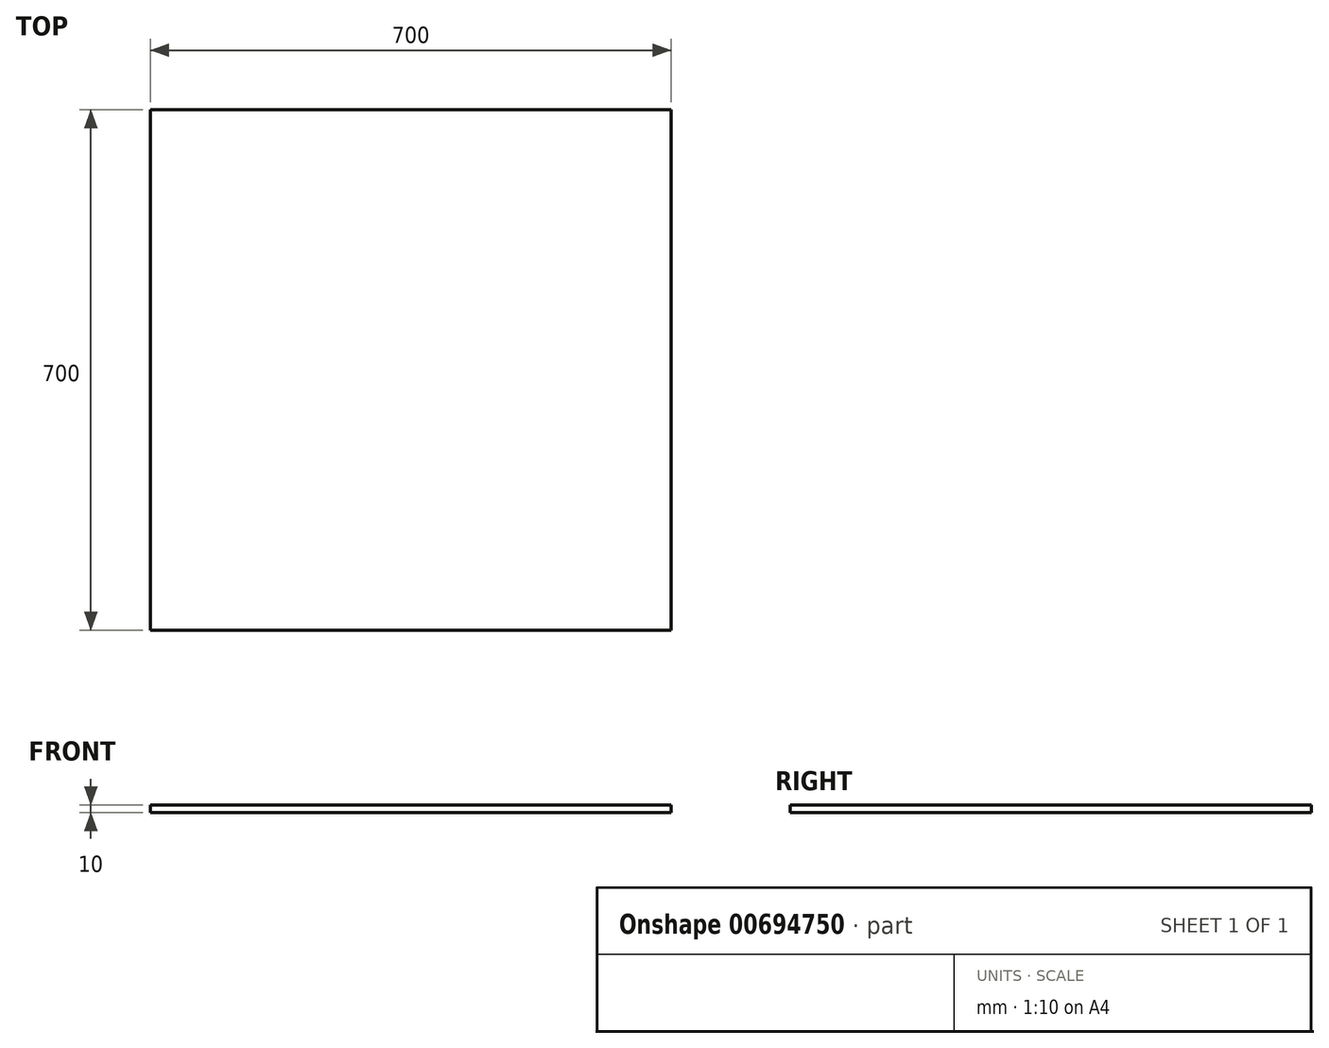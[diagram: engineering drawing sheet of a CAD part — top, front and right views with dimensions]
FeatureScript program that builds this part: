
annotation { "Feature Type Name" : "Feature", "Feature Type Description" : "" }
export const myFeature = defineFeature(function(context is Context, id is Id, definition is map)
    precondition{}
    {
        {
            var Q0;
            Q0=qCreatedBy(makeId("Top.planeOp"),FACE);
            var sketch = newSketch(context, id + "F0", { "sketchPlane" : qUnion([Q0])});
            skLineSegment(sketch, "E0.bottom", {"start": v(350, -350) * mm, "end": v(-350, -350) * mm});
            skLineSegment(sketch, "E0.top", {"start": v(350, 350) * mm, "end": v(-350, 350) * mm});
            skLineSegment(sketch, "E0.left", {"start": v(350, -350) * mm, "end": v(350, 350) * mm});
            skLineSegment(sketch, "E0.right", {"start": v(-350, -350) * mm, "end": v(-350, 350) * mm});
            skPoint(sketch, "E0.middle", {"position": v(0, 0) * mm});
            skSolve(sketch);
        }
        {
            var Q0;
            Q0 = qSketchRegion(id + "F0", true);
            extrude(context, id + "F1", {"entities" : qUnion([Q0]), "endBound" : BoundingType.SYMMETRIC, "depth" : 10 * mm, "offsetDistance" : 25.4 * mm});
        }
    });
